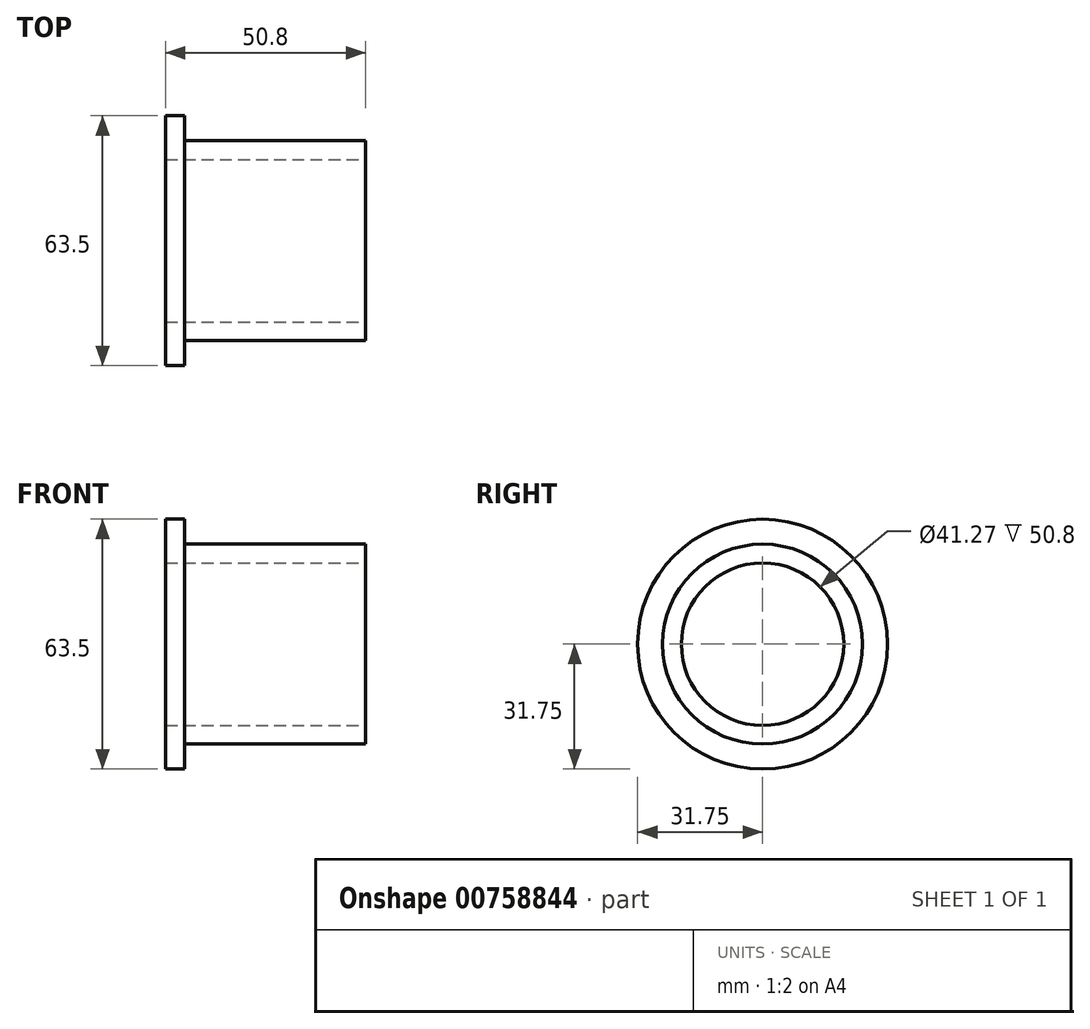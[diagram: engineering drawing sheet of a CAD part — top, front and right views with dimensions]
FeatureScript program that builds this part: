
annotation { "Feature Type Name" : "Feature", "Feature Type Description" : "" }
export const myFeature = defineFeature(function(context is Context, id is Id, definition is map)
    precondition{}
    {
        {
            var Q0;
            Q0=qCreatedBy(makeId("Right.planeOp"),FACE);
            var sketch = newSketch(context, id + "F0", { "sketchPlane" : qUnion([Q0])});
            skCircle(sketch, "E0", {"center": v(0, 0) * mm, "radius": 31.75 * mm});
            skSolve(sketch);
        }
        {
            var Q0;
            Q0=makeQuery(id+"F0.imprint","IMPRINT",FACE,{"disambiguationData":[TD([[makeQuery(id+"F0.imprint","IMPRINT",EDGE,{"derivedFrom":sQuery(id+"F0.wireOp",EDGE,"E0")}),1.0]])]});
            extrude(context, id + "F1", {"entities" : qUnion([Q0]), "depth" : 4.76 * mm, "offsetDistance" : 25.4 * mm});
        }
        {
            var Q0;
            Q0=makeQuery(id+"F1.opExtrude","CAP_FACE",FACE,{"disambiguationData":[OSD([sQuery(id+"F0.wireOp",EDGE,"E0")])],"isStart":true});
            var sketch = newSketch(context, id + "F2", { "sketchPlane" : qUnion([Q0])});
            skCircle(sketch, "E1", {"center": v(0, 0) * mm, "radius": 25.4 * mm});
            skSolve(sketch);
        }
        {
            var Q0;
            Q0=makeQuery(id+"F2.imprint","IMPRINT",FACE,{"disambiguationData":[TD([[makeQuery(id+"F2.imprint","IMPRINT",EDGE,{"derivedFrom":sQuery(id+"F2.wireOp",EDGE,"E1")}),1.0]])]});
            extrude(context, id + "F3", {"entities" : qUnion([Q0]), "operationType" : NewBodyOperationType.ADD, "oppositeDirection" : true, "depth" : 50.8 * mm, "offsetDistance" : 25.4 * mm});
        }
        {
            var Q0;
            Q0=makeQuery(id+"F3.opExtrude","CAP_FACE",FACE,{"disambiguationData":[OSD([sQuery(id+"F2.wireOp",EDGE,"E1")])],"isStart":false});
            var sketch = newSketch(context, id + "F4", { "sketchPlane" : qUnion([Q0])});
            skPoint(sketch, "E2", {"position": v(0, 0) * mm});
            skSolve(sketch);
        }
        {
            var Q0;
            Q0=sQuery(id+"F4.wireOp",VERTEX,"E2");
            var Q1;
            Q1=makeQuery(id+"F1.opExtrude","SWEPT_BODY",BODY,{"disambiguationData":[OSD([sQuery(id+"F0.wireOp",EDGE,"E0")])]});
            hole(context, id + "F5", {"style" : HoleStyle.SIMPLE, "endStyle" : HoleEndStyle.THROUGH, "holeDiameter" : 41.27 * mm, "majorDiameter" : 6.35 * mm, "tappedDepth" : 110.49 * mm, "tapClearance" : 3, "startFromSketch" : true, "locations" : qUnion([Q0]), "scope" : qUnion([Q1])});
        }
    });
